# Revit family: IS_ConnectAir_E0749_BIM_FR
name_source: partatom
category: Plumbing Fixtures
revit_build: Autodesk Revit 2017 (Build: 20160225_1515(x64)
units: mm (PartAtom-declared; Revit-internal decimal feet)

## family parameters
Always vertical = No
Cut with Voids When Loaded = No
OmniClass Number = 23.45.05.14.14
OmniClass Title = Sinks/Lavatories
Part Type = Normal
Room Calculation Point = No
Round Connector Dimension = Use Diameter
Shared = No
Work Plane-Based = No

## types (1)
- E074901 - CONNECT AIR COLONNE BLANC BXD
    Accessoires = www.idealspec.fr
    Auteur = Ideal Standard
    BIMobject category = Basins
    BIMobject category code = sanitary-basins
    BIMobject main category = Sanitary
    BIMobject main category code = sanitary
    BOSUseNativeGeometries = 1
    Bim-NomDuProjet = ISI_IdealStandard_LegsPedestalsGridsAndHangers_CONNECT_E074901
    Brand url = www.idealspec.fr
    Caractéristiques = CONNECT AIR PEDSTAL WHITE BXD
    CodeBarre = 5017830514725
    Conformité = NF
    ConseilsDInstallation = 0
    Cost = 0 $
    Couleur = Blanc
    CoûtDeRemplacement = 0
    Date of publishing = 2018_07_24
    DateDeCréation = 2018_07_24
    Description = CONNECT AIR Colonne
    DiamètreÉvacuation = 0
    Dimensions = 165 x 180 x 720 mm
    EAN code = https://5017830514725
    Edition number = 1
    Espace = Interne
    Finition = Blanc
    Forme = Complexe
    Hauteur = 720 mm  [stored 2.3622 ft]
    IFC Classification = Sanitary Terminal
    IfcExportAs = WASHBASINS
    IfcExportType = IfcSanitaryTerminalType
    InformationsProduit = www.idealspec.fr
    Installation instructions = http://www.idealspec.fr
    Largeur = 180 mm
    Longueur = 165 mm
    Manufacturer name = Ideal Standard
    Marque = Ideal Standard
    Material main = Ceramics
    Matériel = Ceramics
    Model = E074901
    NBS Reference Code = 85-45
    NBS Reference Description = Legs, Pedestals, Grids And Hangers
    Nominal height = 0
    Nominal width = 0
    OmniClass Code = 23-21 25 23 15
    OmniClass Description = Pedestals
    Product Guid = 73e0181b-7af9-40ce-9ca6-6847d2f7026e
    Product SKU = E0749
    Product certification = http://www.idealspec.fr
    Product data url = https://bimobject.com
    Product family = CONNECT AIR
    Product group = Pedestal
    Product name = CONNECT AIR PEDSTAL WHITE BXD
    Product url = http://www.idealspec.fr
    Profondeur = 0 mm  [stored 0 ft]
    QR code = http://bimobject.com
    Raccordement = Plomberie
    Révision = 1
    Technical description = http://www.idealspec.fr
    TypeDeLavabo = Pedestal
    URL = www.idealspec.fr
    Uniclass 1.4 Code = L7212
    Uniclass 1.4 Description = Washbasins
    Uniclass 2.0 Code = PR-85-45
    Uniclass 2.0 Description = Legs, Pedestals, Grids And Hangers
    Uniclass 2015 Code = Pr_20_85_47
    Uniclass 2015 Name = Legs, pedestals, hangers and stringers
    Uniclass2015Code = Pr_20_85_47
    Uniclass2015Title = Legs, pedestals, hangers and stringers
    Uniclass2015Version = Products v1.1
    UnitéDeMesure = Millimètres
    UnitéDeTemps = An
    UnitéMonétaire = €
    UrlDuFabricant = www.idealspec.fr
    Version = 1
    Weight Net (Kg) = 8.32
    Youtube clip = http://www.idealspec.fr

note: [stored X ft] marks values corroborated as IEEE doubles in the binary element streams (Revit-internal decimal feet)

## geometry (parser evidence)
native form markers: Sweep x1
no freeform markers — native parametric forms only
